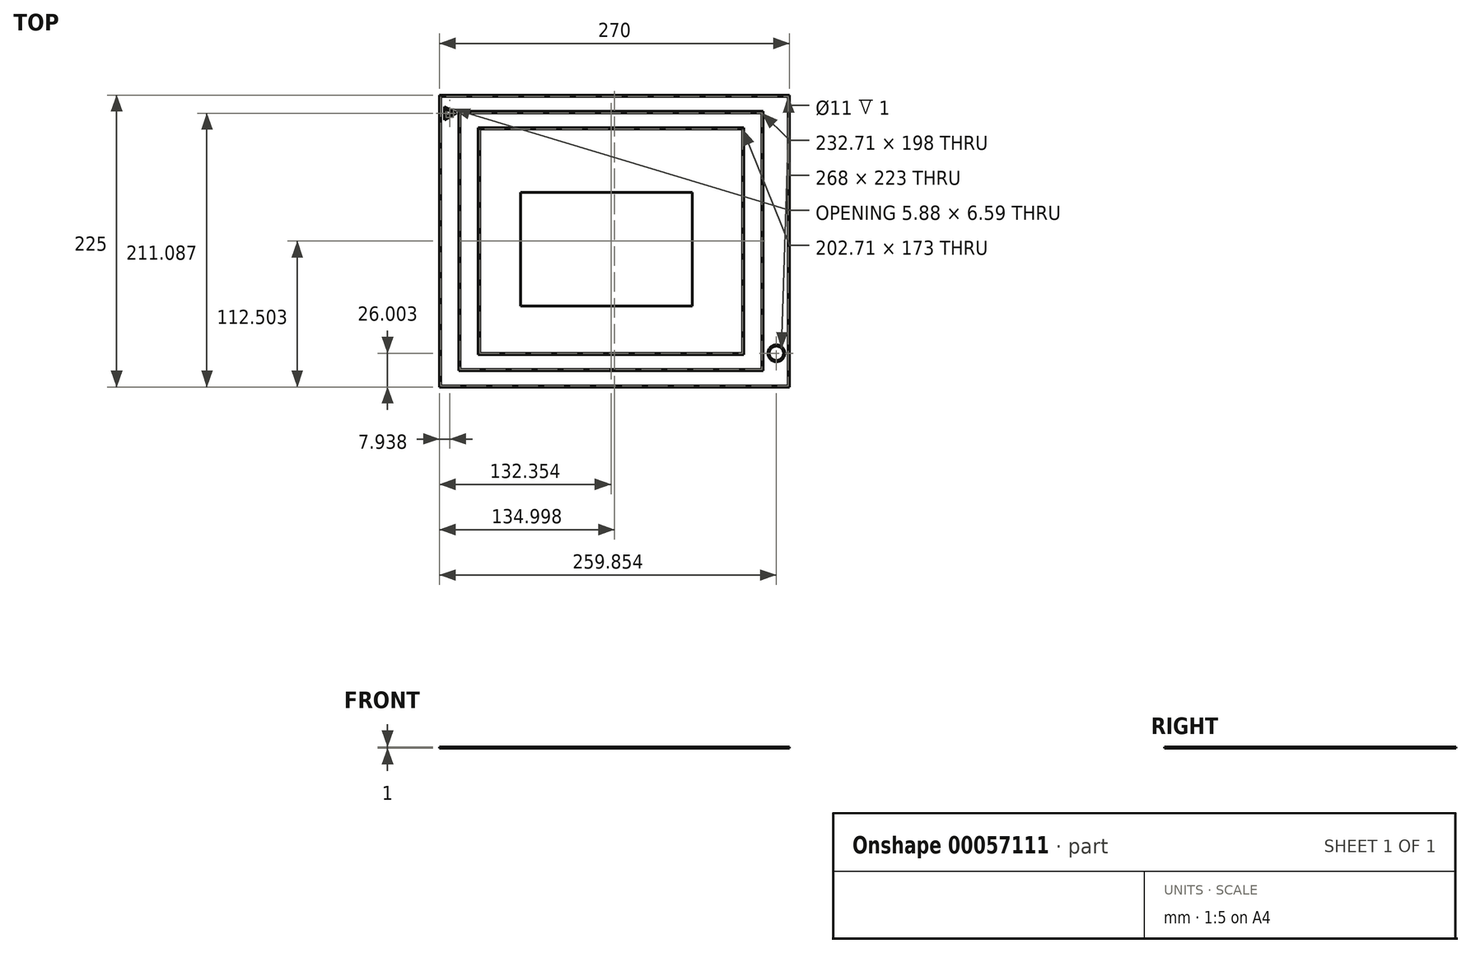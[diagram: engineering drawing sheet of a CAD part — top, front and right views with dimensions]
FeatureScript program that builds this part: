
annotation { "Feature Type Name" : "Feature", "Feature Type Description" : "" }
export const myFeature = defineFeature(function(context is Context, id is Id, definition is map)
    precondition{}
    {
        {
            assignVariable(context, id + "F0", {"name" : "LineHeight", "anyValue" : 1});
        }
        {
            var Q0;
            Q0=qCreatedBy(makeId("Top.planeOp"),FACE);
            var sketch = newSketch(context, id + "F1", { "sketchPlane" : qUnion([Q0])});
            skLineSegment(sketch, "E0.bottom", {"start": v(-91.48, 152.86) * mm, "end": v(178.52, 152.86) * mm});
            skLineSegment(sketch, "E0.top", {"start": v(-91.48, -72.14) * mm, "end": v(178.52, -72.14) * mm});
            skLineSegment(sketch, "E0.left", {"start": v(-91.48, 152.86) * mm, "end": v(-91.48, -72.14) * mm});
            skLineSegment(sketch, "E0.right", {"start": v(178.52, 152.86) * mm, "end": v(178.52, -72.14) * mm});
            skLineSegment(sketch, "E1.bottom", {"start": v(-76.48, 140.36) * mm, "end": v(158.23, 140.36) * mm});
            skLineSegment(sketch, "E1.top", {"start": v(-76.48, -59.64) * mm, "end": v(158.23, -59.64) * mm});
            skLineSegment(sketch, "E1.left", {"start": v(-76.48, 140.36) * mm, "end": v(-76.48, -59.64) * mm});
            skLineSegment(sketch, "E1.right", {"start": v(158.23, 140.36) * mm, "end": v(158.23, -59.64) * mm});
            skLineSegment(sketch, "E2.bottom", {"start": v(-61.48, 127.86) * mm, "end": v(143.23, 127.86) * mm});
            skLineSegment(sketch, "E2.top", {"start": v(-61.48, -47.14) * mm, "end": v(143.23, -47.14) * mm});
            skLineSegment(sketch, "E2.left", {"start": v(-61.48, 127.86) * mm, "end": v(-61.48, -47.14) * mm});
            skLineSegment(sketch, "E2.right", {"start": v(143.23, 127.86) * mm, "end": v(143.23, -47.14) * mm});
            skLineSegment(sketch, "E3.bottom", {"start": v(-28.98, 77.86) * mm, "end": v(103.52, 77.86) * mm});
            skLineSegment(sketch, "E3.top", {"start": v(-28.98, -9.64) * mm, "end": v(103.52, -9.64) * mm});
            skLineSegment(sketch, "E3.left", {"start": v(-28.98, 77.86) * mm, "end": v(-28.98, -9.64) * mm});
            skLineSegment(sketch, "E3.right", {"start": v(103.52, 77.86) * mm, "end": v(103.52, -9.64) * mm});
            skLineSegment(sketch, "E4", {"start": v(-87.48, 143.86) * mm, "end": v(-87.48, 133.86) * mm});
            skLineSegment(sketch, "E5", {"start": v(-87.48, 133.86) * mm, "end": v(-78.55, 139.36) * mm});
            skLineSegment(sketch, "E6", {"start": v(-78.55, 139.36) * mm, "end": v(-87.48, 143.86) * mm});
            skCircle(sketch, "E7", {"center": v(168.37, -46.14) * mm, "radius": 6.5 * mm});
            skLineSegment(sketch, "E8", {"start": v(158.23, -46.14) * mm, "end": v(178.52, -46.14) * mm, "construction": true});
            skLineSegment(sketch, "E9", {"start": v(-90.48, 151.86) * mm, "end": v(177.52, 151.86) * mm});
            skLineSegment(sketch, "E10", {"start": v(177.52, 151.86) * mm, "end": v(177.52, -71.14) * mm});
            skLineSegment(sketch, "E11", {"start": v(177.52, -71.14) * mm, "end": v(-90.48, -71.14) * mm});
            skLineSegment(sketch, "E12", {"start": v(-90.48, -71.14) * mm, "end": v(-90.48, 151.86) * mm});
            skLineSegment(sketch, "E13", {"start": v(-75.48, 139.36) * mm, "end": v(157.23, 139.36) * mm});
            skLineSegment(sketch, "E14", {"start": v(157.23, 139.36) * mm, "end": v(157.23, -58.64) * mm});
            skLineSegment(sketch, "E15", {"start": v(157.23, -58.64) * mm, "end": v(-75.48, -58.64) * mm});
            skLineSegment(sketch, "E16", {"start": v(-75.48, -58.64) * mm, "end": v(-75.48, 139.36) * mm});
            skLineSegment(sketch, "E17", {"start": v(-60.48, 126.86) * mm, "end": v(142.23, 126.86) * mm});
            skLineSegment(sketch, "E18", {"start": v(142.23, 126.86) * mm, "end": v(142.23, -46.14) * mm});
            skLineSegment(sketch, "E19", {"start": v(142.23, -46.14) * mm, "end": v(-60.48, -46.14) * mm});
            skLineSegment(sketch, "E20", {"start": v(-60.48, -46.14) * mm, "end": v(-60.48, 126.86) * mm});
            skCircle(sketch, "E21", {"center": v(168.37, -46.14) * mm, "radius": 5.5 * mm});
            skLineSegment(sketch, "E22", {"start": v(-86.48, 142.24) * mm, "end": v(-80.6, 139.28) * mm});
            skPoint(sketch, "E22.startSnap0", {"position": v(-84.41, 142.24) * mm});
            skLineSegment(sketch, "E23", {"start": v(-80.6, 139.28) * mm, "end": v(-86.48, 135.65) * mm});
            skLineSegment(sketch, "E24", {"start": v(-86.48, 135.65) * mm, "end": v(-86.48, 142.24) * mm});
            skSolve(sketch);
        }
        {
            var Q0;
            Q0=makeQuery(id+"F1.imprint","IMPRINT",FACE,{"disambiguationData":[TD([[makeQuery(id+"F1.imprint","IMPRINT",EDGE,{"derivedFrom":sQuery(id+"F1.wireOp",EDGE,"E0.bottom")}),-1.0]])]});
            var Q1;
            Q1=makeQuery(id+"F1.imprint","IMPRINT",FACE,{"disambiguationData":[TD([[makeQuery(id+"F1.imprint","IMPRINT",EDGE,{"derivedFrom":sQuery(id+"F1.wireOp",EDGE,"E1.bottom")}),-1.0]])]});
            var Q2;
            Q2=makeQuery(id+"F1.imprint","IMPRINT",FACE,{"disambiguationData":[TD([[makeQuery(id+"F1.imprint","IMPRINT",EDGE,{"derivedFrom":sQuery(id+"F1.wireOp",EDGE,"E2.bottom")}),-1.0]])]});
            var Q3;
            Q3=makeQuery(id+"F1.imprint","IMPRINT",FACE,{"disambiguationData":[TD([[makeQuery(id+"F1.imprint","IMPRINT",EDGE,{"derivedFrom":sQuery(id+"F1.wireOp",EDGE,"E7")}),1.0]])]});
            var Q4;
            Q4=makeQuery(id+"F1.imprint","IMPRINT",FACE,{"disambiguationData":[TD([[makeQuery(id+"F1.imprint","IMPRINT",EDGE,{"derivedFrom":sQuery(id+"F1.wireOp",EDGE,"E3.bottom")}),-1.0]])]});
            var Q5;
            Q5=makeQuery(id+"F1.imprint","IMPRINT",FACE,{"disambiguationData":[TD([[makeQuery(id+"F1.imprint","IMPRINT",EDGE,{"derivedFrom":sQuery(id+"F1.wireOp",EDGE,"E4")}),1.0]])]});
            extrude(context, id + "F2", {"entities" : qUnion([Q0, Q1, Q2, Q3, Q4, Q5]), "depth" : (getVariable(context, 'LineHeight')) * mm, "offsetDistance" : 25 * mm});
        }
    });
